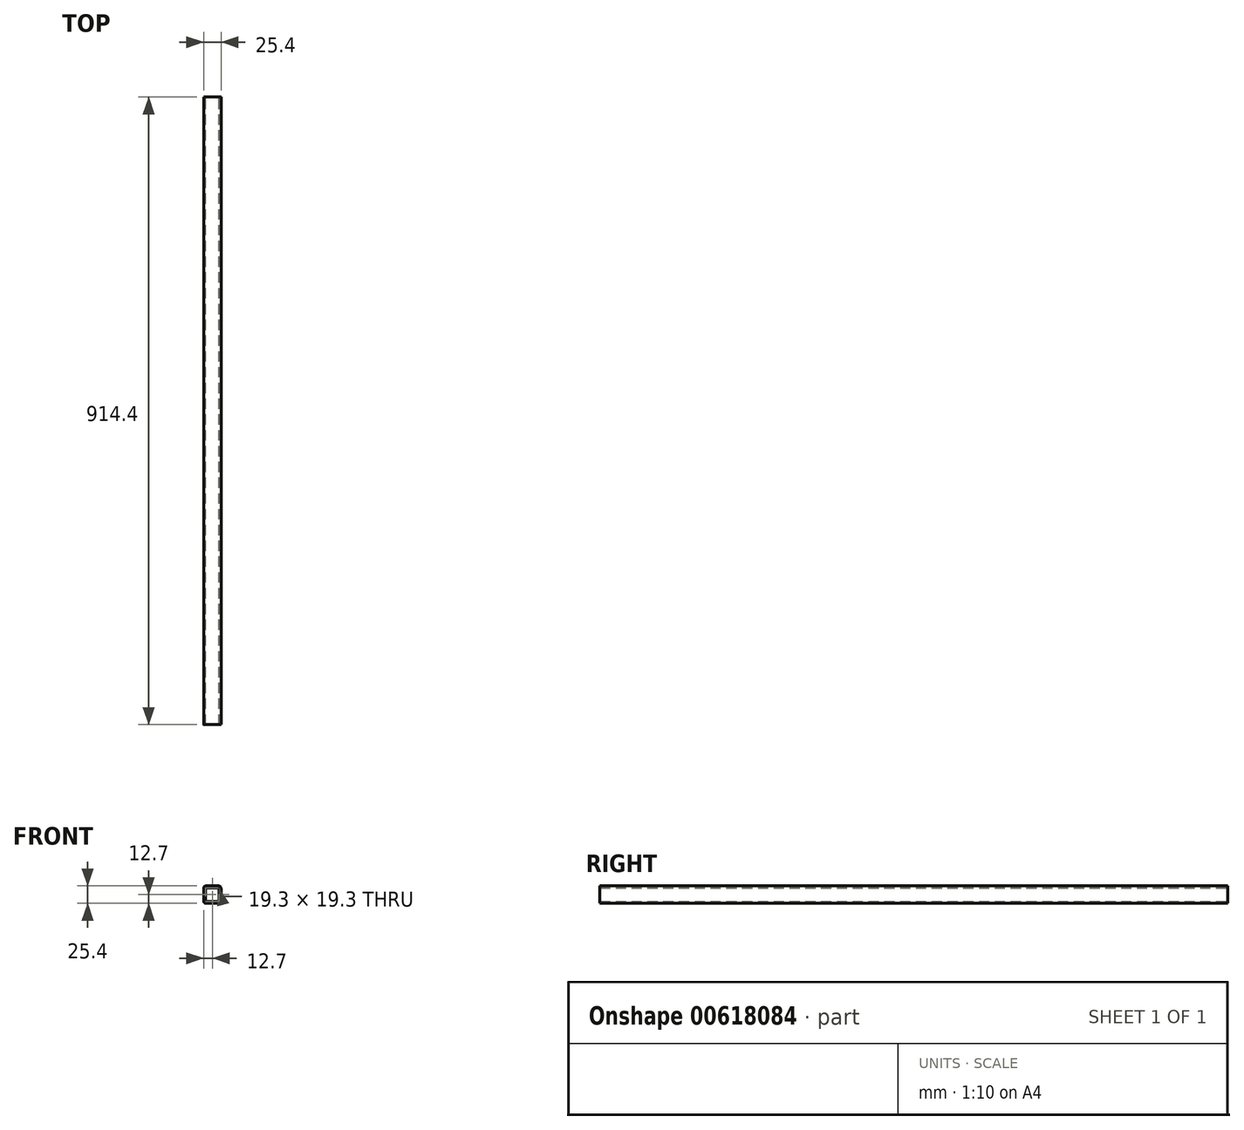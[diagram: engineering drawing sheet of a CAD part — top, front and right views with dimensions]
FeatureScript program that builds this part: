
annotation { "Feature Type Name" : "Feature", "Feature Type Description" : "" }
export const myFeature = defineFeature(function(context is Context, id is Id, definition is map)
    precondition{}
    {
        {
            var Q0;
            Q0=qCreatedBy(makeId("Front.planeOp"),FACE);
            var sketch = newSketch(context, id + "F0", { "sketchPlane" : qUnion([Q0])});
            skLineSegment(sketch, "E0.top", {"start": v(9.4, -12.7) * mm, "end": v(-9.4, -12.7) * mm});
            skLineSegment(sketch, "E0.left", {"start": v(12.7, 9.4) * mm, "end": v(12.7, -9.4) * mm});
            skLineSegment(sketch, "E0.right", {"start": v(-12.7, 9.4) * mm, "end": v(-12.7, -9.4) * mm});
            skPoint(sketch, "E0.middle", {"position": v(0, 0) * mm});
            skPoint(sketch, "E1.visualSharp", {"position": v(-12.7, 12.7) * mm});
            skArc(sketch, "E1.filletArc", {"start": v(-9.4, 12.7) * mm, "mid": v(-11.73, 11.73) * mm, "end": v(-12.7, 9.4) * mm});
            skPoint(sketch, "E2.visualSharp", {"position": v(12.7, 12.7) * mm});
            skArc(sketch, "E2.filletArc", {"start": v(12.7, 9.4) * mm, "mid": v(11.73, 11.73) * mm, "end": v(9.4, 12.7) * mm});
            skPoint(sketch, "E3.visualSharp", {"position": v(12.7, -12.7) * mm});
            skArc(sketch, "E3.filletArc", {"start": v(9.4, -12.7) * mm, "mid": v(11.73, -11.73) * mm, "end": v(12.7, -9.4) * mm});
            skPoint(sketch, "E4.visualSharp", {"position": v(-12.7, -12.7) * mm});
            skArc(sketch, "E4.filletArc", {"start": v(-12.7, -9.4) * mm, "mid": v(-11.73, -11.73) * mm, "end": v(-9.4, -12.7) * mm});
            skLineSegment(sketch, "E5", {"start": v(-9.4, 12.7) * mm, "end": v(9.4, 12.7) * mm});
            skLineSegment(sketch, "E6.0", {"start": v(-9.65, 9.65) * mm, "end": v(9.65, 9.65) * mm});
            skLineSegment(sketch, "E6.1", {"start": v(-9.65, 9.65) * mm, "end": v(-9.65, -9.65) * mm});
            skLineSegment(sketch, "E6.2", {"start": v(9.65, -9.65) * mm, "end": v(-9.65, -9.65) * mm});
            skLineSegment(sketch, "E6.3", {"start": v(9.65, 9.65) * mm, "end": v(9.65, -9.65) * mm});
            skSolve(sketch);
        }
        {
            var Q0;
            Q0 = qSketchRegion(id + "F0", true);
            extrude(context, id + "F1", {"entities" : qUnion([Q0]), "depth" : 914.4 * mm, "offsetDistance" : 25.4 * mm});
        }
    });
